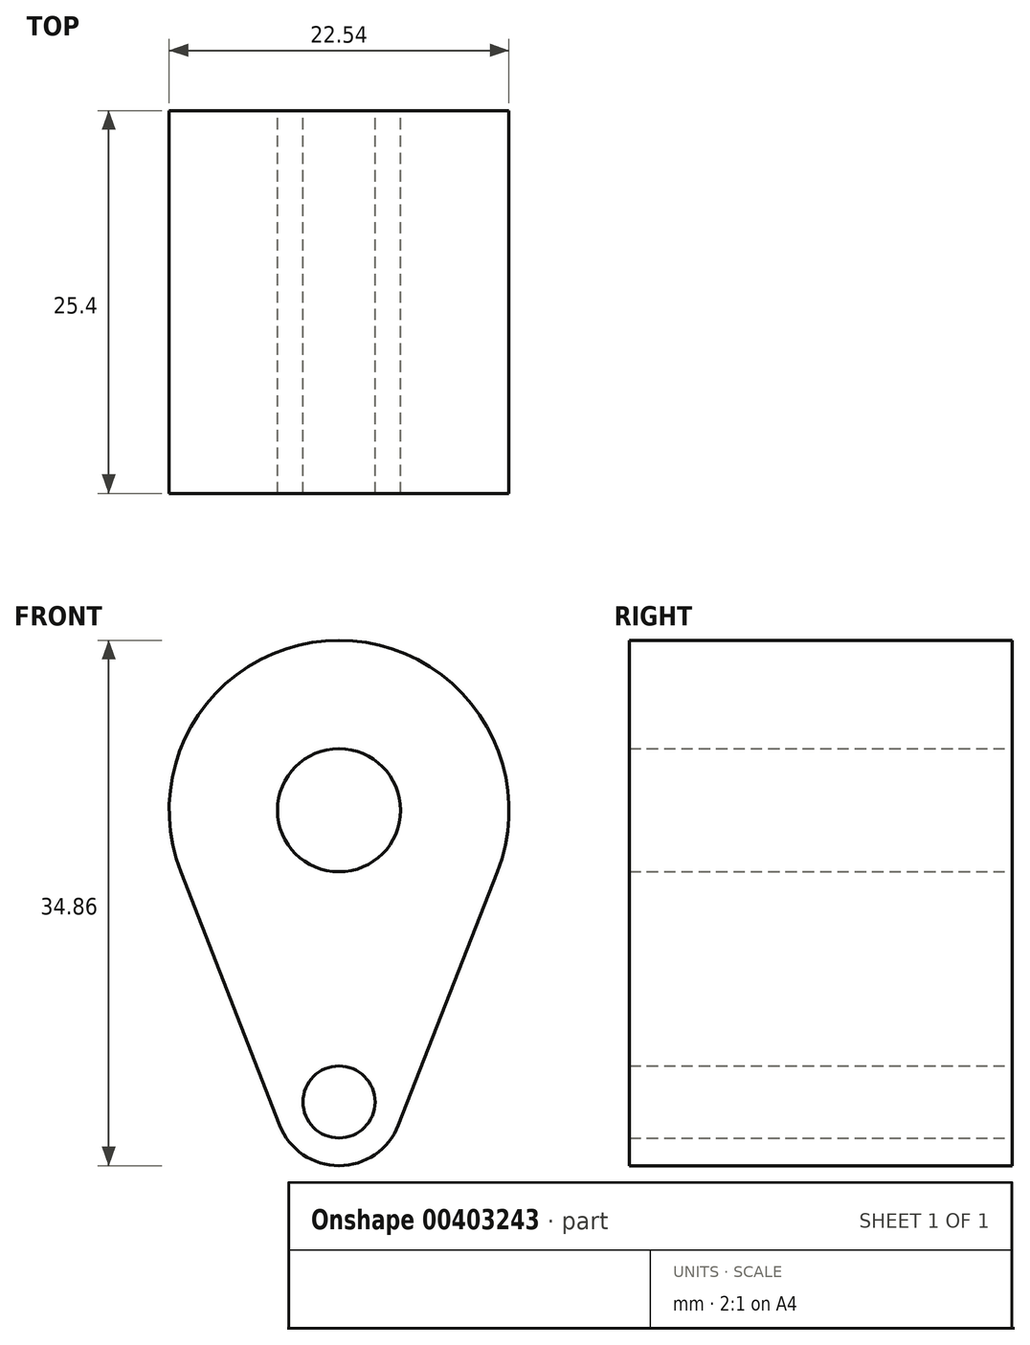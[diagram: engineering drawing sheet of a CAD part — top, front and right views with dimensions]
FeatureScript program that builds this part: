
annotation { "Feature Type Name" : "Feature", "Feature Type Description" : "" }
export const myFeature = defineFeature(function(context is Context, id is Id, definition is map)
    precondition{}
    {
        {
            var Q0;
            Q0=qCreatedBy(makeId("Front.planeOp"),FACE);
            var sketch = newSketch(context, id + "F0", { "sketchPlane" : qUnion([Q0])});
            skArc(sketch, "E0", {"start": v(28.91, 22.07) * mm, "mid": v(18.41, 37.45) * mm, "end": v(7.91, 22.07) * mm});
            skArc(sketch, "E1", {"start": v(14.47, 5.28) * mm, "mid": v(18.41, 2.59) * mm, "end": v(22.35, 5.28) * mm});
            skLineSegment(sketch, "E2", {"start": v(7.91, 22.07) * mm, "end": v(14.47, 5.28) * mm});
            skLineSegment(sketch, "E3.MirrorCS", {"start": v(28.91, 22.07) * mm, "end": v(22.35, 5.28) * mm});
            skCircle(sketch, "E4", {"center": v(18.41, 26.17) * mm, "radius": 4.08 * mm});
            skCircle(sketch, "E5", {"center": v(18.41, 6.82) * mm, "radius": 2.39 * mm});
            skSolve(sketch);
        }
        {
            var Q0;
            Q0=makeQuery(id+"F0.imprint","IMPRINT",FACE,{"disambiguationData":[TD([[makeQuery(id+"F0.imprint","IMPRINT",EDGE,{"derivedFrom":sQuery(id+"F0.wireOp",EDGE,"E0")}),1.0]])]});
            extrude(context, id + "F1", {"entities" : qUnion([Q0]), "depth" : 25.4 * mm});
        }
    });
